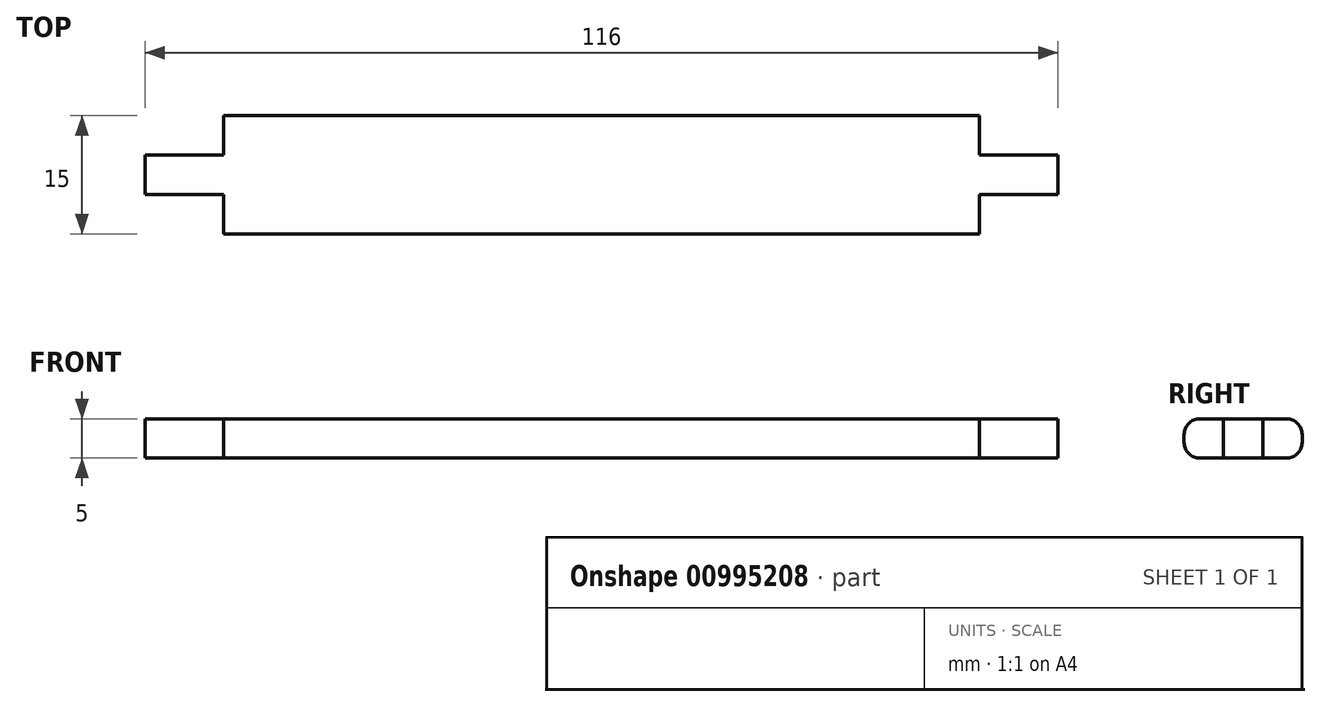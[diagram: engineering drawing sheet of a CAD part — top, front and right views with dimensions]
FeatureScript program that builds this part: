
annotation { "Feature Type Name" : "Feature", "Feature Type Description" : "" }
export const myFeature = defineFeature(function(context is Context, id is Id, definition is map)
    precondition{}
    {
        {
            var Q0;
            Q0=qCreatedBy(makeId("Right.planeOp"),FACE);
            var sketch = newSketch(context, id + "F0", { "sketchPlane" : qUnion([Q0])});
            skLineSegment(sketch, "E0.bottom", {"start": v(-0.54, -1.6) * mm, "end": v(-15.54, -1.6) * mm});
            skLineSegment(sketch, "E0.top", {"start": v(-0.54, 3.4) * mm, "end": v(-15.54, 3.4) * mm});
            skLineSegment(sketch, "E0.left", {"start": v(-0.54, -1.6) * mm, "end": v(-0.54, 3.4) * mm});
            skLineSegment(sketch, "E0.right", {"start": v(-15.54, -1.6) * mm, "end": v(-15.54, 3.4) * mm});
            skPoint(sketch, "E0.middle", {"position": v(-8.04, 0.9) * mm});
            skSolve(sketch);
        }
        {
            var Q0;
            Q0=makeQuery(id+"F0.imprint","IMPRINT",FACE,{"disambiguationData":[TD([[makeQuery(id+"F0.imprint","IMPRINT",EDGE,{"derivedFrom":sQuery(id+"F0.wireOp",EDGE,"E0.bottom")}),-1.0]])]});
            extrude(context, id + "F1", {"entities" : qUnion([Q0]), "depth" : 100 * mm, "offsetDistance" : 25 * mm});
        }
        {
            var Q0;
            Q0=makeQuery(id+"F1.opExtrude","CAP_FACE",FACE,{"disambiguationData":[OSD([sQuery(id+"F0.wireOp",EDGE,"E0.bottom"),sQuery(id+"F0.wireOp",EDGE,"E0.top"),sQuery(id+"F0.wireOp",EDGE,"E0.left"),sQuery(id+"F0.wireOp",EDGE,"E0.right")])],"isStart":false});
            var sketch = newSketch(context, id + "F2", { "sketchPlane" : qUnion([Q0])});
            skLineSegment(sketch, "E1.bottom", {"start": v(-10.54, -1.6) * mm, "end": v(-5.54, -1.6) * mm});
            skLineSegment(sketch, "E1.top", {"start": v(-10.54, 3.4) * mm, "end": v(-5.54, 3.4) * mm});
            skLineSegment(sketch, "E1.left", {"start": v(-10.54, -1.6) * mm, "end": v(-10.54, 3.4) * mm});
            skLineSegment(sketch, "E1.right", {"start": v(-5.54, -1.6) * mm, "end": v(-5.54, 3.4) * mm});
            skSolve(sketch);
        }
        {
            var Q0;
            Q0=makeQuery(id+"F2.imprint","IMPRINT",FACE,{"disambiguationData":[TD([[makeQuery(id+"F2.imprint","IMPRINT",EDGE,{"derivedFrom":sQuery(id+"F2.wireOp",EDGE,"E1.bottom")}),-1.0]])]});
            extrude(context, id + "F3", {"entities" : qUnion([Q0]), "operationType" : NewBodyOperationType.ADD, "depth" : 10 * mm, "offsetDistance" : 25 * mm});
        }
        {
            var Q0;
            Q0=makeQuery(id+"F1.opExtrude","CAP_FACE",FACE,{"disambiguationData":[OSD([sQuery(id+"F0.wireOp",EDGE,"E0.bottom"),sQuery(id+"F0.wireOp",EDGE,"E0.top"),sQuery(id+"F0.wireOp",EDGE,"E0.left"),sQuery(id+"F0.wireOp",EDGE,"E0.right")])],"isStart":true});
            var sketch = newSketch(context, id + "F4", { "sketchPlane" : qUnion([Q0])});
            skLineSegment(sketch, "E2.bottom", {"start": v(5.54, -1.6) * mm, "end": v(10.54, -1.6) * mm});
            skLineSegment(sketch, "E2.top", {"start": v(5.54, 3.4) * mm, "end": v(10.54, 3.4) * mm});
            skLineSegment(sketch, "E2.left", {"start": v(5.54, -1.6) * mm, "end": v(5.54, 3.4) * mm});
            skLineSegment(sketch, "E2.right", {"start": v(10.54, -1.6) * mm, "end": v(10.54, 3.4) * mm});
            skSolve(sketch);
        }
        {
            var Q0;
            Q0=makeQuery(id+"F4.imprint","IMPRINT",FACE,{"disambiguationData":[TD([[makeQuery(id+"F4.imprint","IMPRINT",EDGE,{"derivedFrom":sQuery(id+"F4.wireOp",EDGE,"E2.bottom")}),1.0]])]});
            extrude(context, id + "F5", {"entities" : qUnion([Q0]), "operationType" : NewBodyOperationType.ADD, "depth" : 10 * mm, "offsetDistance" : 25 * mm});
        }
        {
            var Q0;
            {var subQ0=sQuery(id+"F0.wireOp",EDGE,"E0.top");var subQ1=sQuery(id+"F0.wireOp",EDGE,"E0.right");var subQ2=sQuery(id+"F0.wireOp",EDGE,"E0.bottom");Q0=makeQuery(id+"F3.boolean.opBoolean","SPLIT",FACE,{"disambiguationData":[TD([makeQuery(id+"F1.opExtrude","SWEPT_FACE",FACE,{"disambiguationData":[OSD([subQ1])]})])],"derivedFrom":makeQuery(id+"F1.opExtrude","CAP_FACE",FACE,{"disambiguationData":[OSD([subQ2,subQ0,sQuery(id+"F0.wireOp",EDGE,"E0.left"),subQ1])],"isStart":false})});}
            var Q1;
            {var subQ0=sQuery(id+"F0.wireOp",EDGE,"E0.left");var subQ1=sQuery(id+"F0.wireOp",EDGE,"E0.top");var subQ2=sQuery(id+"F0.wireOp",EDGE,"E0.bottom");Q1=makeQuery(id+"F3.boolean.opBoolean","SPLIT",FACE,{"disambiguationData":[TD([makeQuery(id+"F1.opExtrude","SWEPT_FACE",FACE,{"disambiguationData":[OSD([subQ0])]})])],"derivedFrom":makeQuery(id+"F1.opExtrude","CAP_FACE",FACE,{"disambiguationData":[OSD([subQ2,subQ1,subQ0,sQuery(id+"F0.wireOp",EDGE,"E0.right")])],"isStart":false})});}
            var Q2;
            Q2=makeQuery(id+"F3.opExtrude","CAP_FACE",FACE,{"disambiguationData":[OSD([sQuery(id+"F2.wireOp",EDGE,"E1.bottom"),sQuery(id+"F2.wireOp",EDGE,"E1.top"),sQuery(id+"F2.wireOp",EDGE,"E1.left"),sQuery(id+"F2.wireOp",EDGE,"E1.right")])],"isStart":false});
            extrude(context, id + "F6", {"entities" : qUnion([Q0, Q1, Q2]), "operationType" : NewBodyOperationType.REMOVE, "oppositeDirection" : true, "depth" : 4 * mm, "offsetDistance" : 25 * mm});
        }
        {
            var Q0;
            Q0=makeQuery(id+"F1.opExtrude","SWEPT_EDGE",EDGE,{"disambiguationData":[OSD([sQuery(id+"F0.wireOp",EDGE,"E0.top"),sQuery(id+"F0.wireOp",EDGE,"E0.right")])]});
            var Q1;
            Q1=makeQuery(id+"F1.opExtrude","SWEPT_EDGE",EDGE,{"disambiguationData":[OSD([sQuery(id+"F0.wireOp",EDGE,"E0.top"),sQuery(id+"F0.wireOp",EDGE,"E0.left")])]});
            var Q2;
            Q2=makeQuery(id+"F1.opExtrude","SWEPT_EDGE",EDGE,{"disambiguationData":[OSD([sQuery(id+"F0.wireOp",EDGE,"E0.bottom"),sQuery(id+"F0.wireOp",EDGE,"E0.left")])]});
            var Q3;
            Q3=makeQuery(id+"F1.opExtrude","SWEPT_EDGE",EDGE,{"disambiguationData":[OSD([sQuery(id+"F0.wireOp",EDGE,"E0.bottom"),sQuery(id+"F0.wireOp",EDGE,"E0.right")])]});
            fillet(context, id + "F7", {"entities" : qUnion([Q0, Q1, Q2, Q3]), "radius" : 2 * mm, "tangentPropagation" : true, "allowEdgeOverflow" : false});
        }
    });
